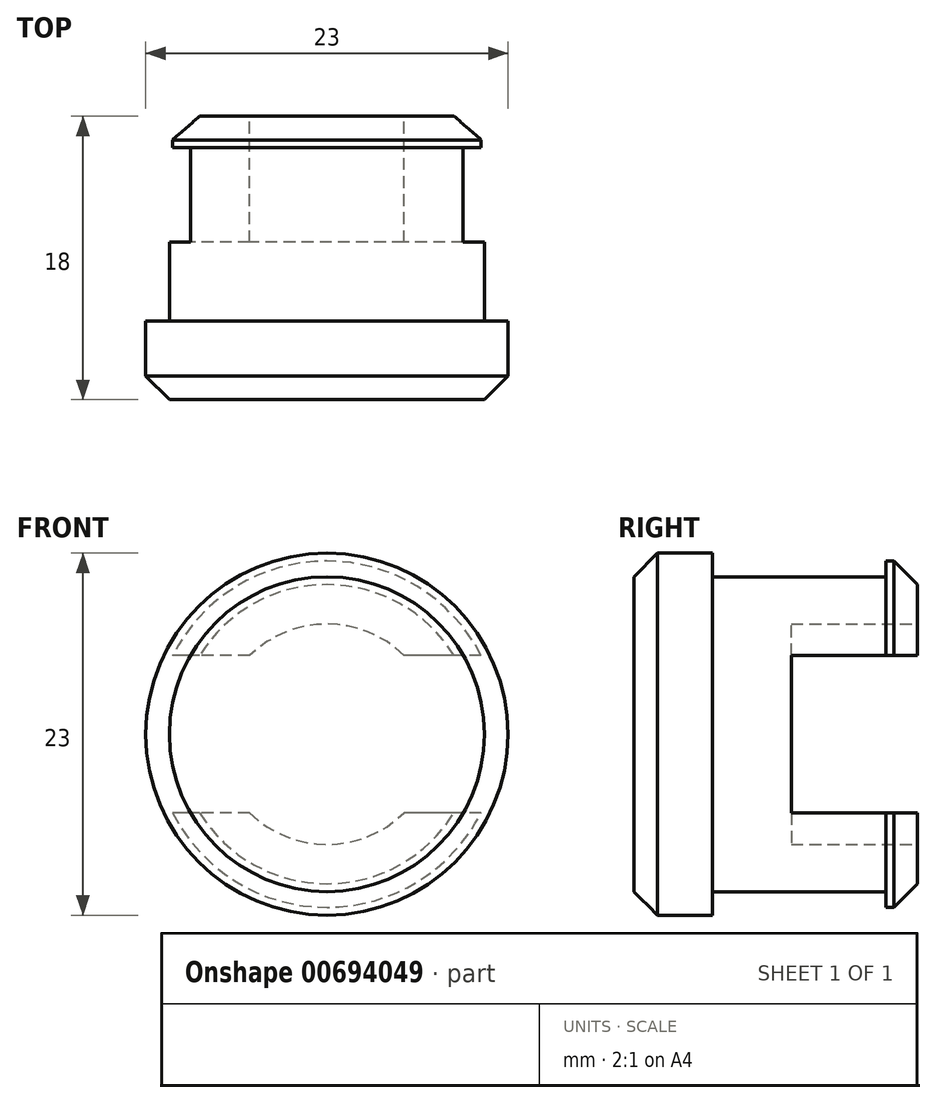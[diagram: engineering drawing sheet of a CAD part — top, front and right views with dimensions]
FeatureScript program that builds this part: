
annotation { "Feature Type Name" : "Feature", "Feature Type Description" : "" }
export const myFeature = defineFeature(function(context is Context, id is Id, definition is map)
    precondition{}
    {
        {
            var Q0;
            Q0=qCreatedBy(makeId("Front.planeOp"),FACE);
            var sketch = newSketch(context, id + "F0", { "sketchPlane" : qUnion([Q0])});
            skCircle(sketch, "E0", {"center": v(0, 0) * mm, "radius": 11.5 * mm});
            skSolve(sketch);
        }
        {
            var Q0;
            Q0=makeQuery(id+"F0.imprint","IMPRINT",FACE,{"disambiguationData":[TD([[makeQuery(id+"F0.imprint","IMPRINT",EDGE,{"derivedFrom":sQuery(id+"F0.wireOp",EDGE,"E0")}),1.0]])]});
            extrude(context, id + "F1", {"entities" : qUnion([Q0]), "depth" : 5 * mm, "offsetDistance" : 25 * mm});
        }
        {
            var Q0;
            Q0=makeQuery(id+"F1.opExtrude","CAP_FACE",FACE,{"disambiguationData":[OSD([sQuery(id+"F0.wireOp",EDGE,"E0")])],"isStart":true});
            var sketch = newSketch(context, id + "F2", { "sketchPlane" : qUnion([Q0])});
            skCircle(sketch, "E1", {"center": v(0, 0) * mm, "radius": 10 * mm});
            skSolve(sketch);
        }
        {
            var Q0;
            Q0 = qSketchRegion(id + "F2", true);
            extrude(context, id + "F3", {"entities" : qUnion([Q0]), "operationType" : NewBodyOperationType.ADD, "depth" : 11 * mm, "offsetDistance" : 25 * mm});
        }
        {
            var Q0;
            Q0=makeQuery(id+"F3.opExtrude","CAP_FACE",FACE,{"disambiguationData":[OSD([sQuery(id+"F2.wireOp",EDGE,"E1")])],"isStart":false});
            var sketch = newSketch(context, id + "F4", { "sketchPlane" : qUnion([Q0])});
            skCircle(sketch, "E2", {"center": v(0, 0) * mm, "radius": 11 * mm});
            skSolve(sketch);
        }
        {
            var Q0;
            Q0 = qSketchRegion(id + "F4", true);
            extrude(context, id + "F5", {"entities" : qUnion([Q0]), "operationType" : NewBodyOperationType.ADD, "depth" : 2 * mm, "offsetDistance" : 25 * mm});
        }
        {
            var Q0;
            Q0=makeQuery(id+"F5.opExtrude","CAP_EDGE",EDGE,{"disambiguationData":[OSD([sQuery(id+"F4.wireOp",EDGE,"E2")])],"isStart":false});
            chamfer(context, id + "F6", {"entities" : qUnion([Q0]), "width" : 1.5 * mm, "tangentPropagation" : true});
        }
        {
            var Q0;
            Q0=makeQuery(id+"F1.opExtrude","CAP_EDGE",EDGE,{"disambiguationData":[OSD([sQuery(id+"F0.wireOp",EDGE,"E0")])],"isStart":false});
            chamfer(context, id + "F7", {"entities" : qUnion([Q0]), "width" : 1.5 * mm, "tangentPropagation" : true});
        }
        {
            var Q0;
            Q0=makeQuery(id+"F5.opExtrude","CAP_FACE",FACE,{"disambiguationData":[OSD([sQuery(id+"F4.wireOp",EDGE,"E2")])],"isStart":false});
            var sketch = newSketch(context, id + "F8", { "sketchPlane" : qUnion([Q0])});
            skLineSegment(sketch, "E3.bottom", {"start": v(-17.5, 5) * mm, "end": v(-4.9, 5) * mm});
            skLineSegment(sketch, "E3.top", {"start": v(-17.5, -5) * mm, "end": v(-4.9, -5) * mm});
            skLineSegment(sketch, "E3.left", {"start": v(-17.5, 5) * mm, "end": v(-17.5, -5) * mm});
            skLineSegment(sketch, "E3.right", {"start": v(17.5, 5) * mm, "end": v(17.5, -5) * mm});
            skPoint(sketch, "E3.middle", {"position": v(0, 0) * mm});
            skArc(sketch, "E4", {"start": v(-4.9, -5) * mm, "mid": v(0, -7) * mm, "end": v(4.9, -5) * mm});
            skLineSegment(sketch, "E5.trimOffspring", {"start": v(4.9, 5) * mm, "end": v(17.5, 5) * mm});
            skLineSegment(sketch, "E6.trimOffspring", {"start": v(4.9, -5) * mm, "end": v(17.5, -5) * mm});
            skArc(sketch, "E7.trimOffspring", {"start": v(4.9, 5) * mm, "mid": v(0, 7) * mm, "end": v(-4.9, 5) * mm});
            skSolve(sketch);
        }
        {
            var Q0;
            {var subQ0=sQuery(id+"F8.wireOp",EDGE,"E3.left");Q0=makeQuery(id+"F8.imprint","IMPRINT",FACE,{"disambiguationData":[TD([[makeQuery(id+"F8.imprint","IMPRINT",EDGE,{"derivedFrom":subQ0}),1.0]])]});}
            var Q1;
            {var subQ0=sQuery(id+"F8.wireOp",EDGE,"E3.right");Q1=makeQuery(id+"F8.imprint","IMPRINT",FACE,{"disambiguationData":[TD([[makeQuery(id+"F8.imprint","IMPRINT",EDGE,{"derivedFrom":subQ0}),-1.0]])]});}
            var Q2;
            {var subQ5=sQuery(id+"F8.wireOp",EDGE,"E4");Q2=makeQuery(id+"F8.imprint","IMPRINT",FACE,{"disambiguationData":[TD([[makeQuery(id+"F8.imprint","IMPRINT",EDGE,{"derivedFrom":subQ5}),1.0]])]});}
            extrude(context, id + "F9", {"entities" : qUnion([Q0, Q1, Q2]), "operationType" : NewBodyOperationType.REMOVE, "oppositeDirection" : true, "depth" : 8 * mm, "offsetDistance" : 25 * mm});
        }
    });
